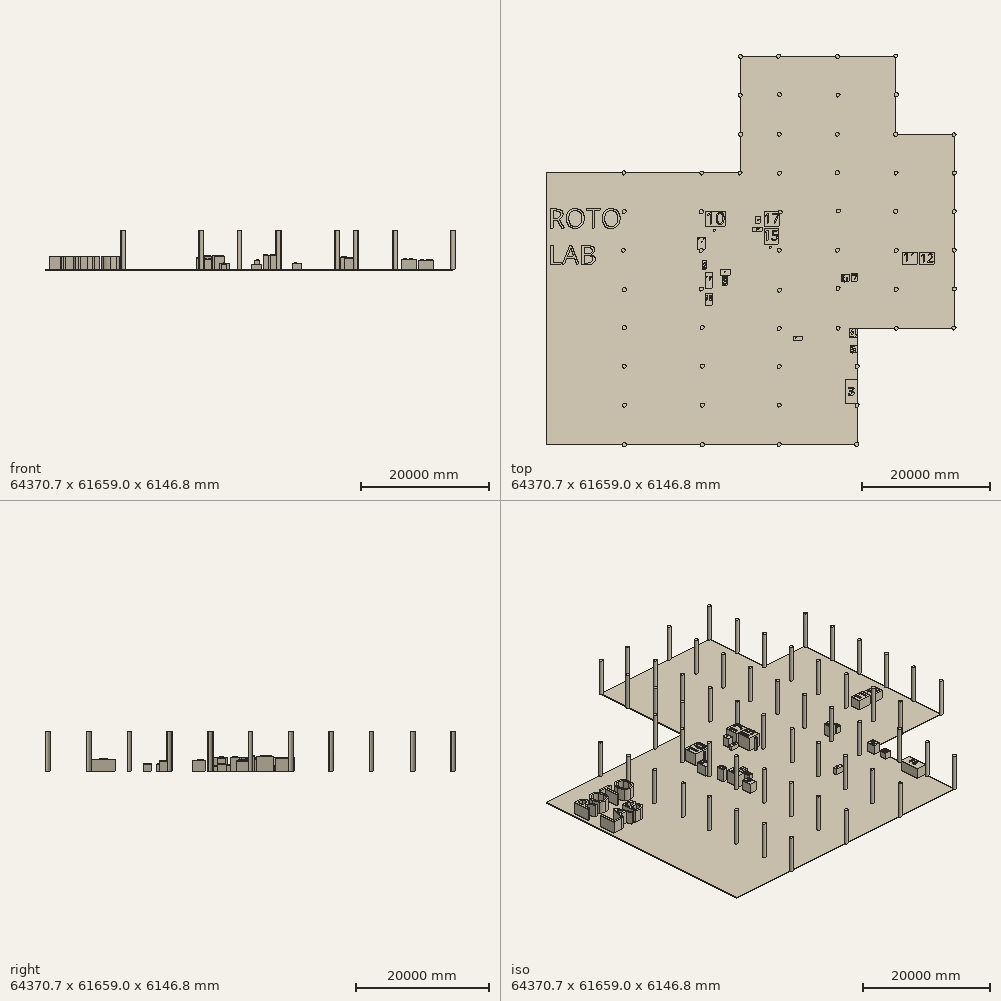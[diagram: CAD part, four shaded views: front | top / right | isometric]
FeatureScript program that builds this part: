
annotation { "Feature Type Name" : "Feature", "Feature Type Description" : "" }
export const myFeature = defineFeature(function(context is Context, id is Id, definition is map)
    precondition{}
    {
        {
            var Q0;
            Q0=qCreatedBy(makeId("Top.planeOp"),FACE);
            var sketch = newSketch(context, id + "F0", { "sketchPlane" : qUnion([Q0])});
            skLineSegment(sketch, "E0", {"start": v(15728, 0) * mm, "end": v(30968, 0) * mm});
            skLineSegment(sketch, "E1", {"start": v(30968, 0) * mm, "end": v(30968, 30480) * mm});
            skLineSegment(sketch, "E2", {"start": v(30968, 30480) * mm, "end": v(21824, 30480) * mm});
            skLineSegment(sketch, "E3", {"start": v(21824, 30480) * mm, "end": v(21824, 42672) * mm});
            skLineSegment(sketch, "E4", {"start": v(-33040, 24384) * mm, "end": v(-33040, 0) * mm});
            skPoint(sketch, "E5", {"position": v(0, 0) * mm});
            skLineSegment(sketch, "E6", {"start": v(-33040, 24384) * mm, "end": v(-2560, 24384) * mm});
            skLineSegment(sketch, "E7", {"start": v(-2560, 24384) * mm, "end": v(-2560, 42672) * mm});
            skLineSegment(sketch, "E8", {"start": v(-2560, 42672) * mm, "end": v(21824, 42672) * mm});
            skLineSegment(sketch, "E9", {"start": v(15728, 0) * mm, "end": v(15728, -18288) * mm});
            skLineSegment(sketch, "E10", {"start": v(15728, -18288) * mm, "end": v(-33040, -18288) * mm});
            skLineSegment(sketch, "E11", {"start": v(-33040, 0) * mm, "end": v(-33040, -18288) * mm});
            skSolve(sketch);
        }
        {
            var Q0;
            Q0 = qSketchRegion(id + "F0", true);
            extrude(context, id + "F1", {"entities" : qUnion([Q0]), "depth" : 50.8 * mm, "offsetDistance" : 25.4 * mm});
        }
        {
            var Q0;
            Q0=makeQuery(id+"F1.opExtrude","CAP_FACE",FACE,{"disambiguationData":[OSD([sQuery(id+"F0.wireOp",EDGE,"E0"),sQuery(id+"F0.wireOp",EDGE,"E1"),sQuery(id+"F0.wireOp",EDGE,"E2"),sQuery(id+"F0.wireOp",EDGE,"E3"),sQuery(id+"F0.wireOp",EDGE,"EMs3Cac7-QPGr-bt8L-WwCN-rmf20JCazhHY"),sQuery(id+"F0.wireOp",EDGE,"psXAcYbY-NMwD-U9ZH-Obsj-Xogxew4PaL97"),sQuery(id+"F0.wireOp",EDGE,"jVNAj40w-TGht-tEG7-xvlJ-PyNoEMkw6fTJ"),sQuery(id+"F0.wireOp",EDGE,"E4")])],"isStart":false});
            var sketch = newSketch(context, id + "F2", { "sketchPlane" : qUnion([Q0])});
            skText(sketch, "E12", { "text": "ROTO \nLAB", "fontName": "OpenSans-Regular.ttf"});
            const initialGuessF2  = {"E12": [-32.77265, 15.6997, 1, 0, 3.04753]};
            skSetInitialGuess(sketch, initialGuessF2);
            skSolve(sketch);
        }
        {
            var Q0;
            Q0 = qSketchRegion(id + "F2", true);
            extrude(context, id + "F3", {"entities" : qUnion([Q0]), "depth" : 2057.4 * mm, "offsetDistance" : 25.4 * mm});
        }
        {
            var Q0;
            {var subQ0=sQuery(id+"F0.wireOp",EDGE,"E2");var subQ1=sQuery(id+"F0.wireOp",EDGE,"E4");var subQ2=sQuery(id+"F0.wireOp",EDGE,"jVNAj40w-TGht-tEG7-xvlJ-PyNoEMkw6fTJ");var subQ3=sQuery(id+"F0.wireOp",EDGE,"psXAcYbY-NMwD-U9ZH-Obsj-Xogxew4PaL97");var subQ4=sQuery(id+"F0.wireOp",EDGE,"EMs3Cac7-QPGr-bt8L-WwCN-rmf20JCazhHY");var subQ5=sQuery(id+"F0.wireOp",EDGE,"E0");var subQ6=sQuery(id+"F0.wireOp",EDGE,"E3");var subQ7=sQuery(id+"F0.wireOp",EDGE,"E1");Q0=makeQuery(id+"F3.boolean.opBoolean","SPLIT",FACE,{"disambiguationData":[TD([makeQuery(id+"F1.opExtrude","SWEPT_FACE",FACE,{"disambiguationData":[OSD([subQ5])]})])],"derivedFrom":makeQuery(id+"F1.opExtrude","CAP_FACE",FACE,{"disambiguationData":[OSD([subQ5,subQ7,subQ0,subQ6,subQ4,subQ3,subQ2,subQ1])],"isStart":false})});}
            var sketch = newSketch(context, id + "F4", { "sketchPlane" : qUnion([Q0])});
            skPoint(sketch, "E13", {"position": v(-20848, 6096) * mm});
            skPoint(sketch, "E14", {"position": v(-20848, 12192) * mm});
            skPoint(sketch, "E15", {"position": v(-20848, 18288) * mm});
            skPoint(sketch, "E16.middle", {"position": v(-20848, 24384) * mm});
            skPoint(sketch, "E17.MirrorP", {"position": v(-8656, 24384) * mm});
            skPoint(sketch, "E18.MirrorP", {"position": v(-8656, 18288) * mm});
            skPoint(sketch, "E19.MirrorP", {"position": v(-8656, 12192) * mm});
            skPoint(sketch, "E20.MirrorP", {"position": v(-8656, 6096) * mm});
            skPoint(sketch, "E21", {"position": v(-2560, 24384) * mm});
            skPoint(sketch, "E22", {"position": v(-2560, 30480) * mm});
            skPoint(sketch, "E23", {"position": v(-2560, 36576) * mm});
            skPoint(sketch, "E24", {"position": v(-2560, 42672) * mm});
            skPoint(sketch, "E25.MirrorP", {"position": v(3536, 24384) * mm});
            skPoint(sketch, "E26.MirrorP", {"position": v(3536, 18288) * mm});
            skPoint(sketch, "E27.MirrorP", {"position": v(3536, 12192) * mm});
            skPoint(sketch, "E28.MirrorP", {"position": v(3536, 6096) * mm});
            skPoint(sketch, "E29.MirrorP", {"position": v(-2538.5, 30490.61) * mm});
            skPoint(sketch, "E30.MirrorP", {"position": v(-2618.75, 36589.82) * mm});
            skPoint(sketch, "E31.MirrorP", {"position": v(-2567.19, 42656.06) * mm});
            skPoint(sketch, "E32", {"position": v(3536, 30487.97) * mm});
            skPoint(sketch, "E33", {"position": v(3536, 36576) * mm});
            skPoint(sketch, "E34", {"position": v(3536, 42672) * mm});
            skPoint(sketch, "E35", {"position": v(30968, 0) * mm});
            skPoint(sketch, "E36", {"position": v(12680, 36576) * mm});
            skPoint(sketch, "E37", {"position": v(12680, 30483.98) * mm});
            skPoint(sketch, "E38", {"position": v(12680, 24384) * mm});
            skPoint(sketch, "E39", {"position": v(12680, 18288) * mm});
            skPoint(sketch, "E40", {"position": v(12680, 12192) * mm});
            skPoint(sketch, "E41", {"position": v(12680, 6096) * mm});
            skPoint(sketch, "E42", {"position": v(21824, 6096) * mm});
            skPoint(sketch, "E43", {"position": v(21824, 12192) * mm});
            skPoint(sketch, "E44", {"position": v(21824, 18288) * mm});
            skPoint(sketch, "E45", {"position": v(21824, 24384) * mm});
            skPoint(sketch, "E46", {"position": v(21824, 36576) * mm});
            skPoint(sketch, "E47", {"position": v(21824, 42672) * mm});
            skPoint(sketch, "E48", {"position": v(30968, 30480) * mm});
            skPoint(sketch, "E49", {"position": v(30968, 24384) * mm});
            skPoint(sketch, "E50.MirrorP", {"position": v(3550.78, 30482.18) * mm});
            skPoint(sketch, "E51.MirrorP", {"position": v(3476.16, 36549.2) * mm});
            skPoint(sketch, "E52.MirrorP", {"position": v(3533.6, 42706.6) * mm});
            skPoint(sketch, "E53.MirrorP", {"position": v(12678, 36632.63) * mm});
            skPoint(sketch, "E54", {"position": v(12680, 42672) * mm});
            skPoint(sketch, "E55.MirrorP", {"position": v(12678.61, 42676.51) * mm});
            skPoint(sketch, "E56.MirrorP", {"position": v(12678.59, 30476.38) * mm});
            skPoint(sketch, "E57.MirrorP", {"position": v(12637.8, 24336.72) * mm});
            skPoint(sketch, "E58.MirrorP", {"position": v(12677.36, 18237.22) * mm});
            skPoint(sketch, "E59.MirrorP", {"position": v(12716.92, 12057.46) * mm});
            skPoint(sketch, "E60.MirrorP", {"position": v(12676.14, 6038.18) * mm});
            skPoint(sketch, "E61.MirrorP", {"position": v(12675.55, 99.18) * mm});
            skPoint(sketch, "E62.MirrorP", {"position": v(21795.62, -57.69) * mm});
            skPoint(sketch, "E63.MirrorP", {"position": v(30955.9, -54.02) * mm});
            skPoint(sketch, "E64", {"position": v(30968, 6096) * mm});
            skPoint(sketch, "E65", {"position": v(30968, 12192) * mm});
            skPoint(sketch, "E66", {"position": v(30968, 18288) * mm});
            skPoint(sketch, "E67.MirrorP", {"position": v(21789.02, 6025.7) * mm});
            skPoint(sketch, "E68.MirrorP", {"position": v(21885.2, 12157.88) * mm});
            skPoint(sketch, "E69.MirrorP", {"position": v(21838.03, 18290) * mm});
            skPoint(sketch, "E70.MirrorP", {"position": v(21790.86, 24374.41) * mm});
            skPoint(sketch, "E71", {"position": v(21824, 30480) * mm});
            skPoint(sketch, "E72.MirrorP", {"position": v(21839.24, 30458.86) * mm});
            skPoint(sketch, "E73.MirrorP", {"position": v(21839.86, 36591) * mm});
            skPoint(sketch, "E74.MirrorP", {"position": v(21803.1, 42617.52) * mm});
            skPoint(sketch, "E75.MirrorP", {"position": v(30931.19, 30439.54) * mm});
            skPoint(sketch, "E76.MirrorP", {"position": v(30930.57, 24310.52) * mm});
            skPoint(sketch, "E77.MirrorP", {"position": v(30929.96, 18209.88) * mm});
            skPoint(sketch, "E78.MirrorP", {"position": v(30900.96, 12279.48) * mm});
            skPoint(sketch, "E79.MirrorP", {"position": v(30957.16, 6065.37) * mm});
            skCircle(sketch, "E80", {"center": v(-20799.6, 6015.66) * mm, "radius": 317.5 * mm});
            skCircle(sketch, "E81", {"center": v(-20946.7, 12207.64) * mm, "radius": 317.5 * mm});
            skCircle(sketch, "E82", {"center": v(-20800.82, 18305.22) * mm, "radius": 317.5 * mm});
            skCircle(sketch, "E83", {"center": v(-20859.17, 24373.64) * mm, "radius": 317.5 * mm});
            skCircle(sketch, "E84", {"center": v(-8556.08, 84.7) * mm, "radius": 317.5 * mm});
            skCircle(sketch, "E85", {"center": v(-8721.12, 6149.9) * mm, "radius": 317.5 * mm});
            skCircle(sketch, "E86", {"center": v(-8762.38, 12173.82) * mm, "radius": 317.5 * mm});
            skCircle(sketch, "E87", {"center": v(-8721.12, 18280.26) * mm, "radius": 317.5 * mm});
            skCircle(sketch, "E88", {"center": v(-8638.6, 24345.45) * mm, "radius": 317.5 * mm});
            skCircle(sketch, "E89", {"center": v(-2655.93, 24345.45) * mm, "radius": 317.5 * mm});
            skCircle(sketch, "E90", {"center": v(-2532.15, 30410.63) * mm, "radius": 317.5 * mm});
            skCircle(sketch, "E91", {"center": v(-2614.67, 36558.34) * mm, "radius": 317.5 * mm});
            skCircle(sketch, "E92", {"center": v(-2532.15, 42623.52) * mm, "radius": 317.5 * mm});
            skCircle(sketch, "E93", {"center": v(3409.25, 42706.04) * mm, "radius": 317.5 * mm});
            skCircle(sketch, "E94", {"center": v(3574.3, 36640.86) * mm, "radius": 317.5 * mm});
            skCircle(sketch, "E95", {"center": v(3491.77, 30451.9) * mm, "radius": 317.5 * mm});
            skCircle(sketch, "E96", {"center": v(3574.3, 24304.19) * mm, "radius": 317.5 * mm});
            skCircle(sketch, "E97", {"center": v(3656.81, 18239) * mm, "radius": 317.5 * mm});
            skCircle(sketch, "E98", {"center": v(3491.77, 12256.34) * mm, "radius": 317.5 * mm});
            skCircle(sketch, "E99", {"center": v(3574.3, 5984.85) * mm, "radius": 317.5 * mm});
            skCircle(sketch, "E100", {"center": v(3491.77, -80.33) * mm, "radius": 317.5 * mm});
            skCircle(sketch, "E101", {"center": v(12733.96, 2.19) * mm, "radius": 317.5 * mm});
            skCircle(sketch, "E102", {"center": v(12733.96, 6273.67) * mm, "radius": 317.5 * mm});
            skCircle(sketch, "E103", {"center": v(12692.7, 12256.34) * mm, "radius": 317.5 * mm});
            skCircle(sketch, "E104", {"center": v(12816.48, 18404.04) * mm, "radius": 317.5 * mm});
            skCircle(sketch, "E105", {"center": v(12651.44, 24386.7) * mm, "radius": 317.5 * mm});
            skCircle(sketch, "E106", {"center": v(12651.44, 30410.63) * mm, "radius": 317.5 * mm});
            skCircle(sketch, "E107", {"center": v(12752.19, 36600.89) * mm, "radius": 317.5 * mm});
            skCircle(sketch, "E108", {"center": v(12653.7, 42639.29) * mm, "radius": 317.5 * mm});
            skCircle(sketch, "E109", {"center": v(21813.25, 42717.7) * mm, "radius": 317.5 * mm});
            skCircle(sketch, "E110", {"center": v(21886.85, 36633.47) * mm, "radius": 317.5 * mm});
            skCircle(sketch, "E111", {"center": v(21813.25, 30402.04) * mm, "radius": 317.5 * mm});
            skCircle(sketch, "E112", {"center": v(30964.14, 30352.98) * mm, "radius": 317.5 * mm});
            skCircle(sketch, "E113", {"center": v(21837.78, 24366.87) * mm, "radius": 317.5 * mm});
            skCircle(sketch, "E114", {"center": v(21788.72, 18331.7) * mm, "radius": 317.5 * mm});
            skCircle(sketch, "E115", {"center": v(31013.2, 24366.87) * mm, "radius": 317.5 * mm});
            skCircle(sketch, "E116", {"center": v(30988.67, 18307.17) * mm, "radius": 317.5 * mm});
            skCircle(sketch, "E117", {"center": v(21886.85, 12173.87) * mm, "radius": 317.5 * mm});
            skCircle(sketch, "E118", {"center": v(30964.13, 12247.47) * mm, "radius": 317.5 * mm});
            skCircle(sketch, "E119", {"center": v(21862.32, 6065.1) * mm, "radius": 317.5 * mm});
            skCircle(sketch, "E120", {"center": v(31013.2, 6163.24) * mm, "radius": 317.5 * mm});
            skCircle(sketch, "E121", {"center": v(21911.38, -19.13) * mm, "radius": 317.5 * mm});
            skCircle(sketch, "E122", {"center": v(30939.6, 5.4) * mm, "radius": 317.5 * mm});
            skLineSegment(sketch, "E123", {"start": v(-20799.6, 6015.66) * mm, "end": v(-20799.6, -23105.73) * mm, "construction": true});
            skLineSegment(sketch, "E124", {"start": v(-8556.08, 84.7) * mm, "end": v(-8556.08, -21895.34) * mm, "construction": true});
            skLineSegment(sketch, "E125", {"start": v(3491.77, -80.33) * mm, "end": v(3491.77, -26208.42) * mm, "construction": true});
            skLineSegment(sketch, "E126", {"start": v(-8556.08, 84.7) * mm, "end": v(-20983, 84.7) * mm, "construction": true});
            skLineSegment(sketch, "E127", {"start": v(-33040, -6011.3) * mm, "end": v(15728, -6011.3) * mm, "construction": true});
            skLineSegment(sketch, "E128", {"start": v(-33040, -12107.3) * mm, "end": v(15728, -12107.3) * mm, "construction": true});
            skCircle(sketch, "E129", {"center": v(-20793.8, 82.6) * mm, "radius": 317.5 * mm});
            skCircle(sketch, "E130", {"center": v(-20807.96, -5984.06) * mm, "radius": 317.5 * mm});
            skCircle(sketch, "E131", {"center": v(-20780.45, -12108.35) * mm, "radius": 317.5 * mm});
            skCircle(sketch, "E132", {"center": v(-20805.76, -18297.2) * mm, "radius": 317.5 * mm});
            skCircle(sketch, "E133", {"center": v(-8567.42, -5956.38) * mm, "radius": 317.5 * mm});
            skCircle(sketch, "E134", {"center": v(-8567.42, -12081.94) * mm, "radius": 317.5 * mm});
            skCircle(sketch, "E135", {"center": v(-8553.38, -18285.04) * mm, "radius": 317.5 * mm});
            skCircle(sketch, "E136", {"center": v(3495.9, -18306.32) * mm, "radius": 317.5 * mm});
            skCircle(sketch, "E137", {"center": v(3490.2, -12072.84) * mm, "radius": 317.5 * mm});
            skCircle(sketch, "E138", {"center": v(3511.49, -6029.21) * mm, "radius": 317.5 * mm});
            skCircle(sketch, "E139", {"center": v(15735.52, -5993.42) * mm, "radius": 317.5 * mm});
            skCircle(sketch, "E140", {"center": v(15717.62, -12096.79) * mm, "radius": 317.5 * mm});
            skCircle(sketch, "E141", {"center": v(15699.72, -18253.85) * mm, "radius": 317.5 * mm});
            skSolve(sketch);
        }
        {
            var Q0;
            Q0 = qSketchRegion(id + "F4", true);
            extrude(context, id + "F5", {"entities" : qUnion([Q0]), "operationType" : NewBodyOperationType.ADD, "depth" : 6096 * mm, "offsetDistance" : 25.4 * mm});
        }
        {
            var Q0;
            {var subQ0=sQuery(id+"F0.wireOp",EDGE,"E2");var subQ1=sQuery(id+"F0.wireOp",EDGE,"E8");var subQ2=sQuery(id+"F0.wireOp",EDGE,"E7");var subQ3=sQuery(id+"F0.wireOp",EDGE,"E6");var subQ4=sQuery(id+"F0.wireOp",EDGE,"E4");var subQ5=sQuery(id+"F0.wireOp",EDGE,"E0");var subQ6=sQuery(id+"F0.wireOp",EDGE,"E3");var subQ7=sQuery(id+"F0.wireOp",EDGE,"E1");Q0=makeQuery(id+"F3.boolean.opBoolean","SPLIT",FACE,{"disambiguationData":[TD([makeQuery(id+"F1.opExtrude","SWEPT_FACE",FACE,{"disambiguationData":[OSD([subQ5])]})])],"derivedFrom":makeQuery(id+"F1.opExtrude","CAP_FACE",FACE,{"disambiguationData":[OSD([subQ5,subQ7,subQ0,subQ6,subQ4,subQ3,subQ2,subQ1])],"isStart":false})});}
            var sketch = newSketch(context, id + "F6", { "sketchPlane" : qUnion([Q0])});
            skLineSegment(sketch, "E142.bottom", {"start": v(-5719.61, 9235.68) * mm, "end": v(-4195.61, 9235.68) * mm});
            skLineSegment(sketch, "E142.top", {"start": v(-5719.61, 8321.28) * mm, "end": v(-4195.61, 8321.28) * mm});
            skLineSegment(sketch, "E142.left", {"start": v(-5719.61, 9235.68) * mm, "end": v(-5719.61, 8321.28) * mm});
            skLineSegment(sketch, "E142.right", {"start": v(-4195.61, 9235.68) * mm, "end": v(-4195.61, 8321.28) * mm});
            skSolve(sketch);
        }
        {
            var Q0;
            Q0 = qSketchRegion(id + "F6", true);
            extrude(context, id + "F7", {"entities" : qUnion([Q0]), "depth" : 990.6 * mm, "offsetDistance" : 25.4 * mm});
        }
        {
            var Q0;
            {var subQ0=sQuery(id+"F0.wireOp",EDGE,"E2");var subQ1=sQuery(id+"F0.wireOp",EDGE,"E8");var subQ2=sQuery(id+"F0.wireOp",EDGE,"E7");var subQ3=sQuery(id+"F0.wireOp",EDGE,"E6");var subQ4=sQuery(id+"F0.wireOp",EDGE,"E4");var subQ5=sQuery(id+"F0.wireOp",EDGE,"E0");var subQ6=sQuery(id+"F0.wireOp",EDGE,"E3");var subQ7=sQuery(id+"F0.wireOp",EDGE,"E1");Q0=makeQuery(id+"F3.boolean.opBoolean","SPLIT",FACE,{"disambiguationData":[TD([makeQuery(id+"F1.opExtrude","SWEPT_FACE",FACE,{"disambiguationData":[OSD([subQ5])]})])],"derivedFrom":makeQuery(id+"F1.opExtrude","CAP_FACE",FACE,{"disambiguationData":[OSD([subQ5,subQ7,subQ0,subQ6,subQ4,subQ3,subQ2,subQ1])],"isStart":false})});}
            var sketch = newSketch(context, id + "F8", { "sketchPlane" : qUnion([Q0])});
            skLineSegment(sketch, "E143.bottom", {"start": v(-8590.4, 10569.5) * mm, "end": v(-7853.8, 10569.5) * mm});
            skLineSegment(sketch, "E143.top", {"start": v(-8590.4, 9172.5) * mm, "end": v(-7853.8, 9172.5) * mm});
            skLineSegment(sketch, "E143.left", {"start": v(-8590.4, 10569.5) * mm, "end": v(-8590.4, 9172.5) * mm});
            skLineSegment(sketch, "E143.right", {"start": v(-7853.8, 10569.5) * mm, "end": v(-7853.8, 9172.5) * mm});
            skSolve(sketch);
        }
        {
            var Q0;
            {var subQ0=sQuery(id+"F0.wireOp",EDGE,"E9");var subQ1=sQuery(id+"F0.wireOp",EDGE,"E8");var subQ2=sQuery(id+"F0.wireOp",EDGE,"E7");var subQ3=sQuery(id+"F0.wireOp",EDGE,"E6");var subQ4=sQuery(id+"F0.wireOp",EDGE,"E11");var subQ5=sQuery(id+"F0.wireOp",EDGE,"E4");var subQ6=sQuery(id+"F0.wireOp",EDGE,"E10");var subQ7=sQuery(id+"F0.wireOp",EDGE,"E0");var subQ8=sQuery(id+"F0.wireOp",EDGE,"E3");var subQ9=sQuery(id+"F0.wireOp",EDGE,"E1");var subQ10=sQuery(id+"F0.wireOp",EDGE,"E2");Q0=makeQuery(id+"F3.boolean.opBoolean","SPLIT",FACE,{"disambiguationData":[TD([makeQuery(id+"F1.opExtrude","SWEPT_FACE",FACE,{"disambiguationData":[OSD([subQ7])]})])],"derivedFrom":makeQuery(id+"F1.opExtrude","CAP_FACE",FACE,{"disambiguationData":[OSD([subQ7,subQ9,subQ10,subQ8,subQ5,subQ3,subQ2,subQ1,subQ0,subQ6,subQ4])],"isStart":false})});}
            var sketch = newSketch(context, id + "F9", { "sketchPlane" : qUnion([Q0])});
            skLineSegment(sketch, "E144.bottom", {"start": v(13899.2, -8121.86) * mm, "end": v(15728, -8121.86) * mm});
            skLineSegment(sketch, "E144.top", {"start": v(13899.2, -11779.46) * mm, "end": v(15728, -11779.46) * mm});
            skLineSegment(sketch, "E144.left", {"start": v(13899.2, -8121.86) * mm, "end": v(13899.2, -11779.46) * mm});
            skLineSegment(sketch, "E144.right", {"start": v(15728, -8121.86) * mm, "end": v(15728, -11779.46) * mm});
            skSolve(sketch);
        }
        {
            var Q0;
            Q0 = qSketchRegion(id + "F9", true);
            extrude(context, id + "F10", {"entities" : qUnion([Q0]), "depth" : 1778 * mm, "offsetDistance" : 25.4 * mm});
        }
        {
            var Q0;
            {var subQ0=sQuery(id+"F0.wireOp",EDGE,"E9");var subQ1=sQuery(id+"F0.wireOp",EDGE,"E8");var subQ2=sQuery(id+"F0.wireOp",EDGE,"E7");var subQ3=sQuery(id+"F0.wireOp",EDGE,"E6");var subQ4=sQuery(id+"F0.wireOp",EDGE,"E11");var subQ5=sQuery(id+"F0.wireOp",EDGE,"E4");var subQ6=sQuery(id+"F0.wireOp",EDGE,"E10");var subQ7=sQuery(id+"F0.wireOp",EDGE,"E0");var subQ8=sQuery(id+"F0.wireOp",EDGE,"E3");var subQ9=sQuery(id+"F0.wireOp",EDGE,"E1");var subQ10=sQuery(id+"F0.wireOp",EDGE,"E2");Q0=makeQuery(id+"F3.boolean.opBoolean","SPLIT",FACE,{"disambiguationData":[TD([makeQuery(id+"F1.opExtrude","SWEPT_FACE",FACE,{"disambiguationData":[OSD([subQ7])]})])],"derivedFrom":makeQuery(id+"F1.opExtrude","CAP_FACE",FACE,{"disambiguationData":[OSD([subQ7,subQ9,subQ10,subQ8,subQ5,subQ3,subQ2,subQ1,subQ0,subQ6,subQ4])],"isStart":false})});}
            var sketch = newSketch(context, id + "F11", { "sketchPlane" : qUnion([Q0])});
            skLineSegment(sketch, "E145.bottom", {"start": v(14508.8, 0) * mm, "end": v(15728, 0) * mm});
            skLineSegment(sketch, "E145.top", {"start": v(14508.8, -1524) * mm, "end": v(15728, -1524) * mm});
            skLineSegment(sketch, "E145.left", {"start": v(14508.8, 0) * mm, "end": v(14508.8, -1524) * mm});
            skLineSegment(sketch, "E145.right", {"start": v(15728, 0) * mm, "end": v(15728, -1524) * mm});
            skSolve(sketch);
        }
        {
            var Q0;
            Q0 = qSketchRegion(id + "F11", true);
            extrude(context, id + "F12", {"entities" : qUnion([Q0]), "depth" : 1524 * mm, "offsetDistance" : 25.4 * mm});
        }
        {
            var Q0;
            {var subQ0=sQuery(id+"F0.wireOp",EDGE,"E9");var subQ1=sQuery(id+"F0.wireOp",EDGE,"E8");var subQ2=sQuery(id+"F0.wireOp",EDGE,"E7");var subQ3=sQuery(id+"F0.wireOp",EDGE,"E6");var subQ4=sQuery(id+"F0.wireOp",EDGE,"E11");var subQ5=sQuery(id+"F0.wireOp",EDGE,"E4");var subQ6=sQuery(id+"F0.wireOp",EDGE,"E10");var subQ7=sQuery(id+"F0.wireOp",EDGE,"E0");var subQ8=sQuery(id+"F0.wireOp",EDGE,"E3");var subQ9=sQuery(id+"F0.wireOp",EDGE,"E1");var subQ10=sQuery(id+"F0.wireOp",EDGE,"E2");Q0=makeQuery(id+"F3.boolean.opBoolean","SPLIT",FACE,{"disambiguationData":[TD([makeQuery(id+"F1.opExtrude","SWEPT_FACE",FACE,{"disambiguationData":[OSD([subQ7])]})])],"derivedFrom":makeQuery(id+"F1.opExtrude","CAP_FACE",FACE,{"disambiguationData":[OSD([subQ7,subQ9,subQ10,subQ8,subQ5,subQ3,subQ2,subQ1,subQ0,subQ6,subQ4])],"isStart":false})});}
            var sketch = newSketch(context, id + "F13", { "sketchPlane" : qUnion([Q0])});
            skLineSegment(sketch, "E146.bottom", {"start": v(14661.2, -2731.45) * mm, "end": v(15728, -2731.45) * mm});
            skLineSegment(sketch, "E146.top", {"start": v(14661.2, -3874.45) * mm, "end": v(15728, -3874.45) * mm});
            skLineSegment(sketch, "E146.left", {"start": v(14661.2, -2731.45) * mm, "end": v(14661.2, -3874.45) * mm});
            skLineSegment(sketch, "E146.right", {"start": v(15728, -2731.45) * mm, "end": v(15728, -3874.45) * mm});
            skSolve(sketch);
        }
        {
            var Q0;
            Q0 = qSketchRegion(id + "F13", true);
            extrude(context, id + "F14", {"entities" : qUnion([Q0]), "depth" : 1041.4 * mm, "offsetDistance" : 25.4 * mm});
        }
        {
            var Q0;
            {var subQ0=sQuery(id+"F0.wireOp",EDGE,"E9");var subQ1=sQuery(id+"F0.wireOp",EDGE,"E8");var subQ2=sQuery(id+"F0.wireOp",EDGE,"E7");var subQ3=sQuery(id+"F0.wireOp",EDGE,"E6");var subQ4=sQuery(id+"F0.wireOp",EDGE,"E11");var subQ5=sQuery(id+"F0.wireOp",EDGE,"E4");var subQ6=sQuery(id+"F0.wireOp",EDGE,"E10");var subQ7=sQuery(id+"F0.wireOp",EDGE,"E0");var subQ8=sQuery(id+"F0.wireOp",EDGE,"E3");var subQ9=sQuery(id+"F0.wireOp",EDGE,"E1");var subQ10=sQuery(id+"F0.wireOp",EDGE,"E2");Q0=makeQuery(id+"F3.boolean.opBoolean","SPLIT",FACE,{"disambiguationData":[TD([makeQuery(id+"F1.opExtrude","SWEPT_FACE",FACE,{"disambiguationData":[OSD([subQ7])]})])],"derivedFrom":makeQuery(id+"F1.opExtrude","CAP_FACE",FACE,{"disambiguationData":[OSD([subQ7,subQ9,subQ10,subQ8,subQ5,subQ3,subQ2,subQ1,subQ0,subQ6,subQ4])],"isStart":false})});}
            var sketch = newSketch(context, id + "F15", { "sketchPlane" : qUnion([Q0])});
            skLineSegment(sketch, "E147.bottom", {"start": v(13343.47, 7272.04) * mm, "end": v(14562.67, 7272.04) * mm});
            skLineSegment(sketch, "E147.top", {"start": v(13343.47, 8491.24) * mm, "end": v(14562.67, 8491.24) * mm});
            skLineSegment(sketch, "E147.left", {"start": v(13343.47, 7272.04) * mm, "end": v(13343.47, 8491.24) * mm});
            skLineSegment(sketch, "E147.right", {"start": v(14562.67, 7272.04) * mm, "end": v(14562.67, 8491.24) * mm});
            skSolve(sketch);
        }
        {
            var Q0;
            Q0 = qSketchRegion(id + "F15", true);
            extrude(context, id + "F16", {"entities" : qUnion([Q0]), "depth" : 1905 * mm, "offsetDistance" : 25.4 * mm});
        }
        {
            var Q0;
            {var subQ0=sQuery(id+"F0.wireOp",EDGE,"E9");var subQ1=sQuery(id+"F0.wireOp",EDGE,"E8");var subQ2=sQuery(id+"F0.wireOp",EDGE,"E7");var subQ3=sQuery(id+"F0.wireOp",EDGE,"E6");var subQ4=sQuery(id+"F0.wireOp",EDGE,"E11");var subQ5=sQuery(id+"F0.wireOp",EDGE,"E4");var subQ6=sQuery(id+"F0.wireOp",EDGE,"E10");var subQ7=sQuery(id+"F0.wireOp",EDGE,"E0");var subQ8=sQuery(id+"F0.wireOp",EDGE,"E3");var subQ9=sQuery(id+"F0.wireOp",EDGE,"E1");var subQ10=sQuery(id+"F0.wireOp",EDGE,"E2");Q0=makeQuery(id+"F3.boolean.opBoolean","SPLIT",FACE,{"disambiguationData":[TD([makeQuery(id+"F1.opExtrude","SWEPT_FACE",FACE,{"disambiguationData":[OSD([subQ7])]})])],"derivedFrom":makeQuery(id+"F1.opExtrude","CAP_FACE",FACE,{"disambiguationData":[OSD([subQ7,subQ9,subQ10,subQ8,subQ5,subQ3,subQ2,subQ1,subQ0,subQ6,subQ4])],"isStart":false})});}
            var sketch = newSketch(context, id + "F17", { "sketchPlane" : qUnion([Q0])});
            skLineSegment(sketch, "E148.bottom", {"start": v(14902.92, 8525.07) * mm, "end": v(15817.32, 8525.07) * mm});
            skLineSegment(sketch, "E148.top", {"start": v(14902.92, 7305.87) * mm, "end": v(15817.32, 7305.87) * mm});
            skLineSegment(sketch, "E148.left", {"start": v(14902.92, 8525.07) * mm, "end": v(14902.92, 7305.87) * mm});
            skLineSegment(sketch, "E148.right", {"start": v(15817.32, 8525.07) * mm, "end": v(15817.32, 7305.87) * mm});
            skSolve(sketch);
        }
        {
            var Q0;
            Q0=makeQuery(id+"F17.imprint","IMPRINT",FACE,{"disambiguationData":[TD([[makeQuery(id+"F17.imprint","IMPRINT",EDGE,{"derivedFrom":sQuery(id+"F17.wireOp",EDGE,"E148.bottom")}),-1.0]])]});
            extrude(context, id + "F18", {"entities" : qUnion([Q0]), "depth" : 1092.2 * mm, "offsetDistance" : 25.4 * mm});
        }
        {
            var Q0;
            Q0=makeQuery(id+"F8.imprint","IMPRINT",FACE,{"disambiguationData":[TD([[makeQuery(id+"F8.imprint","IMPRINT",EDGE,{"derivedFrom":sQuery(id+"F8.wireOp",EDGE,"E143.bottom")}),-1.0]])]});
            extrude(context, id + "F19", {"entities" : qUnion([Q0]), "depth" : 2184.4 * mm, "offsetDistance" : 25.4 * mm});
        }
        {
            var Q0;
            {var subQ0=sQuery(id+"F0.wireOp",EDGE,"E9");var subQ1=sQuery(id+"F0.wireOp",EDGE,"E8");var subQ2=sQuery(id+"F0.wireOp",EDGE,"E7");var subQ3=sQuery(id+"F0.wireOp",EDGE,"E6");var subQ4=sQuery(id+"F0.wireOp",EDGE,"E11");var subQ5=sQuery(id+"F0.wireOp",EDGE,"E4");var subQ6=sQuery(id+"F0.wireOp",EDGE,"E10");var subQ7=sQuery(id+"F0.wireOp",EDGE,"E0");var subQ8=sQuery(id+"F0.wireOp",EDGE,"E3");var subQ9=sQuery(id+"F0.wireOp",EDGE,"E1");var subQ10=sQuery(id+"F0.wireOp",EDGE,"E2");Q0=makeQuery(id+"F3.boolean.opBoolean","SPLIT",FACE,{"disambiguationData":[TD([makeQuery(id+"F1.opExtrude","SWEPT_FACE",FACE,{"disambiguationData":[OSD([subQ7])]})])],"derivedFrom":makeQuery(id+"F1.opExtrude","CAP_FACE",FACE,{"disambiguationData":[OSD([subQ7,subQ9,subQ10,subQ8,subQ5,subQ3,subQ2,subQ1,subQ0,subQ6,subQ4])],"isStart":false})});}
            var sketch = newSketch(context, id + "F20", { "sketchPlane" : qUnion([Q0])});
            skLineSegment(sketch, "E149.bottom", {"start": v(-5361.74, 8182.09) * mm, "end": v(-4574.34, 8182.09) * mm});
            skLineSegment(sketch, "E149.top", {"start": v(-5361.74, 6658.09) * mm, "end": v(-4574.34, 6658.09) * mm});
            skLineSegment(sketch, "E149.left", {"start": v(-5361.74, 8182.09) * mm, "end": v(-5361.74, 6658.09) * mm});
            skLineSegment(sketch, "E149.right", {"start": v(-4574.34, 8182.09) * mm, "end": v(-4574.34, 6658.09) * mm});
            skSolve(sketch);
        }
        {
            var Q0;
            Q0 = qSketchRegion(id + "F20", true);
            extrude(context, id + "F21", {"entities" : qUnion([Q0]), "depth" : 838.2 * mm, "offsetDistance" : 25.4 * mm});
        }
        {
            var Q0;
            Q0=makeQuery(id+"F1.opExtrude","CAP_FACE",FACE,{"disambiguationData":[OSD([sQuery(id+"F0.wireOp",EDGE,"E0"),sQuery(id+"F0.wireOp",EDGE,"E1"),sQuery(id+"F0.wireOp",EDGE,"E2"),sQuery(id+"F0.wireOp",EDGE,"E3"),sQuery(id+"F0.wireOp",EDGE,"E4"),sQuery(id+"F0.wireOp",EDGE,"E6"),sQuery(id+"F0.wireOp",EDGE,"E7"),sQuery(id+"F0.wireOp",EDGE,"E8"),sQuery(id+"F0.wireOp",EDGE,"E9"),sQuery(id+"F0.wireOp",EDGE,"E10"),sQuery(id+"F0.wireOp",EDGE,"E11")])],"isStart":false});
            var sketch = newSketch(context, id + "F22", { "sketchPlane" : qUnion([Q0])});
            skLineSegment(sketch, "E150.bottom", {"start": v(5661.14, -1274.5) * mm, "end": v(7185.14, -1274.5) * mm});
            skLineSegment(sketch, "E150.top", {"start": v(5661.14, -1884.1) * mm, "end": v(7185.14, -1884.1) * mm});
            skLineSegment(sketch, "E150.left", {"start": v(5661.14, -1274.5) * mm, "end": v(5661.14, -1884.1) * mm});
            skLineSegment(sketch, "E150.right", {"start": v(7185.14, -1274.5) * mm, "end": v(7185.14, -1884.1) * mm});
            skSolve(sketch);
        }
        {
            var Q0;
            Q0 = qSketchRegion(id + "F22", true);
            extrude(context, id + "F23", {"entities" : qUnion([Q0]), "depth" : 1016 * mm, "offsetDistance" : 25.4 * mm});
        }
        {
            var Q0;
            Q0=makeQuery(id+"F1.opExtrude","CAP_FACE",FACE,{"disambiguationData":[OSD([sQuery(id+"F0.wireOp",EDGE,"E0"),sQuery(id+"F0.wireOp",EDGE,"E1"),sQuery(id+"F0.wireOp",EDGE,"E2"),sQuery(id+"F0.wireOp",EDGE,"E3"),sQuery(id+"F0.wireOp",EDGE,"E4"),sQuery(id+"F0.wireOp",EDGE,"E6"),sQuery(id+"F0.wireOp",EDGE,"E7"),sQuery(id+"F0.wireOp",EDGE,"E8"),sQuery(id+"F0.wireOp",EDGE,"E9"),sQuery(id+"F0.wireOp",EDGE,"E10"),sQuery(id+"F0.wireOp",EDGE,"E11")])],"isStart":false});
            var sketch = newSketch(context, id + "F24", { "sketchPlane" : qUnion([Q0])});
            skLineSegment(sketch, "E151.bottom", {"start": v(-8019.62, 18366.4) * mm, "end": v(-4971.62, 18366.4) * mm});
            skLineSegment(sketch, "E151.top", {"start": v(-8019.62, 15928) * mm, "end": v(-4971.62, 15928) * mm});
            skLineSegment(sketch, "E151.left", {"start": v(-8019.62, 18366.4) * mm, "end": v(-8019.62, 15928) * mm});
            skLineSegment(sketch, "E151.right", {"start": v(-4971.62, 18366.4) * mm, "end": v(-4971.62, 15928) * mm});
            skSolve(sketch);
        }
        {
            var Q0;
            Q0 = qSketchRegion(id + "F24", true);
            extrude(context, id + "F25", {"entities" : qUnion([Q0]), "depth" : 2057.4 * mm, "offsetDistance" : 25.4 * mm});
        }
        {
            var Q0;
            Q0=makeQuery(id+"F1.opExtrude","CAP_FACE",FACE,{"disambiguationData":[OSD([sQuery(id+"F0.wireOp",EDGE,"E0"),sQuery(id+"F0.wireOp",EDGE,"E1"),sQuery(id+"F0.wireOp",EDGE,"E2"),sQuery(id+"F0.wireOp",EDGE,"E3"),sQuery(id+"F0.wireOp",EDGE,"E4"),sQuery(id+"F0.wireOp",EDGE,"E6"),sQuery(id+"F0.wireOp",EDGE,"E7"),sQuery(id+"F0.wireOp",EDGE,"E8"),sQuery(id+"F0.wireOp",EDGE,"E9"),sQuery(id+"F0.wireOp",EDGE,"E10"),sQuery(id+"F0.wireOp",EDGE,"E11")])],"isStart":false});
            var sketch = newSketch(context, id + "F26", { "sketchPlane" : qUnion([Q0])});
            skLineSegment(sketch, "E152.bottom", {"start": v(22791.92, 11899.81) * mm, "end": v(25230.32, 11899.81) * mm});
            skLineSegment(sketch, "E152.top", {"start": v(22791.92, 10071.01) * mm, "end": v(25230.32, 10071.01) * mm});
            skLineSegment(sketch, "E152.left", {"start": v(22791.92, 11899.81) * mm, "end": v(22791.92, 10071.01) * mm});
            skLineSegment(sketch, "E152.right", {"start": v(25230.32, 11899.81) * mm, "end": v(25230.32, 10071.01) * mm});
            skSolve(sketch);
        }
        {
            var Q0;
            Q0 = qSketchRegion(id + "F26", true);
            extrude(context, id + "F27", {"entities" : qUnion([Q0]), "depth" : 1651 * mm, "offsetDistance" : 25.4 * mm});
        }
        {
            var Q0;
            Q0=makeQuery(id+"F1.opExtrude","CAP_FACE",FACE,{"disambiguationData":[OSD([sQuery(id+"F0.wireOp",EDGE,"E0"),sQuery(id+"F0.wireOp",EDGE,"E1"),sQuery(id+"F0.wireOp",EDGE,"E2"),sQuery(id+"F0.wireOp",EDGE,"E3"),sQuery(id+"F0.wireOp",EDGE,"E4"),sQuery(id+"F0.wireOp",EDGE,"E6"),sQuery(id+"F0.wireOp",EDGE,"E7"),sQuery(id+"F0.wireOp",EDGE,"E8"),sQuery(id+"F0.wireOp",EDGE,"E9"),sQuery(id+"F0.wireOp",EDGE,"E10"),sQuery(id+"F0.wireOp",EDGE,"E11")])],"isStart":false});
            var sketch = newSketch(context, id + "F28", { "sketchPlane" : qUnion([Q0])});
            skLineSegment(sketch, "E153.bottom", {"start": v(25478.95, 11867.2) * mm, "end": v(27917.35, 11867.2) * mm});
            skLineSegment(sketch, "E153.top", {"start": v(25478.95, 10038.4) * mm, "end": v(27917.35, 10038.4) * mm});
            skLineSegment(sketch, "E153.left", {"start": v(25478.95, 11867.2) * mm, "end": v(25478.95, 10038.4) * mm});
            skLineSegment(sketch, "E153.right", {"start": v(27917.35, 11867.2) * mm, "end": v(27917.35, 10038.4) * mm});
            skSolve(sketch);
        }
        {
            var Q0;
            Q0 = qSketchRegion(id + "F28", true);
            extrude(context, id + "F29", {"entities" : qUnion([Q0]), "depth" : 1473.2 * mm, "offsetDistance" : 25.4 * mm});
        }
        {
            var Q0;
            Q0=makeQuery(id+"F1.opExtrude","CAP_FACE",FACE,{"disambiguationData":[OSD([sQuery(id+"F0.wireOp",EDGE,"E0"),sQuery(id+"F0.wireOp",EDGE,"E1"),sQuery(id+"F0.wireOp",EDGE,"E2"),sQuery(id+"F0.wireOp",EDGE,"E3"),sQuery(id+"F0.wireOp",EDGE,"E4"),sQuery(id+"F0.wireOp",EDGE,"E6"),sQuery(id+"F0.wireOp",EDGE,"E7"),sQuery(id+"F0.wireOp",EDGE,"E8"),sQuery(id+"F0.wireOp",EDGE,"E9"),sQuery(id+"F0.wireOp",EDGE,"E10"),sQuery(id+"F0.wireOp",EDGE,"E11")])],"isStart":false});
            var sketch = newSketch(context, id + "F30", { "sketchPlane" : qUnion([Q0])});
            skLineSegment(sketch, "E154.bottom", {"start": v(-9311.37, 14229.33) * mm, "end": v(-8092.17, 14229.33) * mm});
            skLineSegment(sketch, "E154.top", {"start": v(-9311.37, 12400.53) * mm, "end": v(-8092.17, 12400.53) * mm});
            skLineSegment(sketch, "E154.left", {"start": v(-9311.37, 14229.33) * mm, "end": v(-9311.37, 12400.53) * mm});
            skLineSegment(sketch, "E154.right", {"start": v(-8092.17, 14229.33) * mm, "end": v(-8092.17, 12400.53) * mm});
            skSolve(sketch);
        }
        {
            var Q0;
            Q0 = qSketchRegion(id + "F30", true);
            extrude(context, id + "F31", {"entities" : qUnion([Q0]), "depth" : 1778 * mm, "offsetDistance" : 25.4 * mm});
        }
        {
            var Q0;
            Q0=makeQuery(id+"F1.opExtrude","CAP_FACE",FACE,{"disambiguationData":[OSD([sQuery(id+"F0.wireOp",EDGE,"E0"),sQuery(id+"F0.wireOp",EDGE,"E1"),sQuery(id+"F0.wireOp",EDGE,"E2"),sQuery(id+"F0.wireOp",EDGE,"E3"),sQuery(id+"F0.wireOp",EDGE,"E4"),sQuery(id+"F0.wireOp",EDGE,"E6"),sQuery(id+"F0.wireOp",EDGE,"E7"),sQuery(id+"F0.wireOp",EDGE,"E8"),sQuery(id+"F0.wireOp",EDGE,"E9"),sQuery(id+"F0.wireOp",EDGE,"E10"),sQuery(id+"F0.wireOp",EDGE,"E11")])],"isStart":false});
            var sketch = newSketch(context, id + "F32", { "sketchPlane" : qUnion([Q0])});
            skLineSegment(sketch, "E155.bottom", {"start": v(1224.85, 15605.8) * mm, "end": v(3358.45, 15605.8) * mm});
            skLineSegment(sketch, "E155.top", {"start": v(1224.85, 13167.4) * mm, "end": v(3358.45, 13167.4) * mm});
            skLineSegment(sketch, "E155.left", {"start": v(1224.85, 15605.8) * mm, "end": v(1224.85, 13167.4) * mm});
            skLineSegment(sketch, "E155.right", {"start": v(3358.45, 15605.8) * mm, "end": v(3358.45, 13167.4) * mm});
            skSolve(sketch);
        }
        {
            var Q0;
            Q0 = qSketchRegion(id + "F32", true);
            extrude(context, id + "F33", {"entities" : qUnion([Q0]), "depth" : 2286 * mm, "offsetDistance" : 25.4 * mm});
        }
        {
            var Q0;
            Q0=makeQuery(id+"F1.opExtrude","CAP_FACE",FACE,{"disambiguationData":[OSD([sQuery(id+"F0.wireOp",EDGE,"E0"),sQuery(id+"F0.wireOp",EDGE,"E1"),sQuery(id+"F0.wireOp",EDGE,"E2"),sQuery(id+"F0.wireOp",EDGE,"E3"),sQuery(id+"F0.wireOp",EDGE,"E4"),sQuery(id+"F0.wireOp",EDGE,"E6"),sQuery(id+"F0.wireOp",EDGE,"E7"),sQuery(id+"F0.wireOp",EDGE,"E8"),sQuery(id+"F0.wireOp",EDGE,"E9"),sQuery(id+"F0.wireOp",EDGE,"E10"),sQuery(id+"F0.wireOp",EDGE,"E11")])],"isStart":false});
            var sketch = newSketch(context, id + "F34", { "sketchPlane" : qUnion([Q0])});
            skLineSegment(sketch, "E156.bottom", {"start": v(-672, 15848.04) * mm, "end": v(852, 15848.04) * mm});
            skLineSegment(sketch, "E156.top", {"start": v(-672, 15238.44) * mm, "end": v(852, 15238.44) * mm});
            skLineSegment(sketch, "E156.left", {"start": v(-672, 15848.04) * mm, "end": v(-672, 15238.44) * mm});
            skLineSegment(sketch, "E156.right", {"start": v(852, 15848.04) * mm, "end": v(852, 15238.44) * mm});
            skSolve(sketch);
        }
        {
            var Q0;
            Q0 = qSketchRegion(id + "F34", true);
            extrude(context, id + "F35", {"entities" : qUnion([Q0]), "depth" : 762 * mm, "offsetDistance" : 25.4 * mm});
        }
        {
            var Q0;
            Q0=makeQuery(id+"F1.opExtrude","CAP_FACE",FACE,{"disambiguationData":[OSD([sQuery(id+"F0.wireOp",EDGE,"E0"),sQuery(id+"F0.wireOp",EDGE,"E1"),sQuery(id+"F0.wireOp",EDGE,"E2"),sQuery(id+"F0.wireOp",EDGE,"E3"),sQuery(id+"F0.wireOp",EDGE,"E4"),sQuery(id+"F0.wireOp",EDGE,"E6"),sQuery(id+"F0.wireOp",EDGE,"E7"),sQuery(id+"F0.wireOp",EDGE,"E8"),sQuery(id+"F0.wireOp",EDGE,"E9"),sQuery(id+"F0.wireOp",EDGE,"E10"),sQuery(id+"F0.wireOp",EDGE,"E11")])],"isStart":false});
            var sketch = newSketch(context, id + "F36", { "sketchPlane" : qUnion([Q0])});
            skLineSegment(sketch, "E157.bottom", {"start": v(-8146.07, 5381.36) * mm, "end": v(-6926.87, 5381.36) * mm});
            skLineSegment(sketch, "E157.top", {"start": v(-8146.07, 3552.56) * mm, "end": v(-6926.87, 3552.56) * mm});
            skLineSegment(sketch, "E157.left", {"start": v(-8146.07, 5381.36) * mm, "end": v(-8146.07, 3552.56) * mm});
            skLineSegment(sketch, "E157.right", {"start": v(-6926.87, 5381.36) * mm, "end": v(-6926.87, 3552.56) * mm});
            skSolve(sketch);
        }
        {
            var Q0;
            Q0 = qSketchRegion(id + "F36", true);
            extrude(context, id + "F37", {"entities" : qUnion([Q0]), "depth" : 1625.6 * mm, "offsetDistance" : 25.4 * mm});
        }
        {
            var Q0;
            Q0=makeQuery(id+"F1.opExtrude","CAP_FACE",FACE,{"disambiguationData":[OSD([sQuery(id+"F0.wireOp",EDGE,"E0"),sQuery(id+"F0.wireOp",EDGE,"E1"),sQuery(id+"F0.wireOp",EDGE,"E2"),sQuery(id+"F0.wireOp",EDGE,"E3"),sQuery(id+"F0.wireOp",EDGE,"E4"),sQuery(id+"F0.wireOp",EDGE,"E6"),sQuery(id+"F0.wireOp",EDGE,"E7"),sQuery(id+"F0.wireOp",EDGE,"E8"),sQuery(id+"F0.wireOp",EDGE,"E9"),sQuery(id+"F0.wireOp",EDGE,"E10"),sQuery(id+"F0.wireOp",EDGE,"E11")])],"isStart":false});
            var sketch = newSketch(context, id + "F38", { "sketchPlane" : qUnion([Q0])});
            skLineSegment(sketch, "E158.bottom", {"start": v(1177.7, 18375.05) * mm, "end": v(3616.1, 18375.05) * mm});
            skLineSegment(sketch, "E158.top", {"start": v(1177.7, 15936.65) * mm, "end": v(3616.1, 15936.65) * mm});
            skLineSegment(sketch, "E158.left", {"start": v(1177.7, 18375.05) * mm, "end": v(1177.7, 15936.65) * mm});
            skLineSegment(sketch, "E158.right", {"start": v(3616.1, 18375.05) * mm, "end": v(3616.1, 15936.65) * mm});
            skSolve(sketch);
        }
        {
            var Q0;
            Q0 = qSketchRegion(id + "F38", true);
            extrude(context, id + "F39", {"entities" : qUnion([Q0]), "depth" : 2032 * mm, "offsetDistance" : 25.4 * mm});
        }
        {
            var Q0;
            Q0=makeQuery(id+"F1.opExtrude","CAP_FACE",FACE,{"disambiguationData":[OSD([sQuery(id+"F0.wireOp",EDGE,"E0"),sQuery(id+"F0.wireOp",EDGE,"E1"),sQuery(id+"F0.wireOp",EDGE,"E2"),sQuery(id+"F0.wireOp",EDGE,"E3"),sQuery(id+"F0.wireOp",EDGE,"E4"),sQuery(id+"F0.wireOp",EDGE,"E6"),sQuery(id+"F0.wireOp",EDGE,"E7"),sQuery(id+"F0.wireOp",EDGE,"E8"),sQuery(id+"F0.wireOp",EDGE,"E9"),sQuery(id+"F0.wireOp",EDGE,"E10"),sQuery(id+"F0.wireOp",EDGE,"E11")])],"isStart":false});
            var sketch = newSketch(context, id + "F40", { "sketchPlane" : qUnion([Q0])});
            skLineSegment(sketch, "E159.bottom", {"start": v(-287.27, 17594.45) * mm, "end": v(627.13, 17594.45) * mm});
            skLineSegment(sketch, "E159.top", {"start": v(-287.27, 16375.25) * mm, "end": v(627.13, 16375.25) * mm});
            skLineSegment(sketch, "E159.left", {"start": v(-287.27, 17594.45) * mm, "end": v(-287.27, 16375.25) * mm});
            skLineSegment(sketch, "E159.right", {"start": v(627.13, 17594.45) * mm, "end": v(627.13, 16375.25) * mm});
            skSolve(sketch);
        }
        {
            var Q0;
            Q0 = qSketchRegion(id + "F40", true);
            extrude(context, id + "F41", {"entities" : qUnion([Q0]), "depth" : 1524 * mm, "offsetDistance" : 25.4 * mm});
        }
        {
            var Q0;
            Q0=makeQuery(id+"F1.opExtrude","CAP_FACE",FACE,{"disambiguationData":[OSD([sQuery(id+"F0.wireOp",EDGE,"E0"),sQuery(id+"F0.wireOp",EDGE,"E1"),sQuery(id+"F0.wireOp",EDGE,"E2"),sQuery(id+"F0.wireOp",EDGE,"E3"),sQuery(id+"F0.wireOp",EDGE,"E4"),sQuery(id+"F0.wireOp",EDGE,"E6"),sQuery(id+"F0.wireOp",EDGE,"E7"),sQuery(id+"F0.wireOp",EDGE,"E8"),sQuery(id+"F0.wireOp",EDGE,"E9"),sQuery(id+"F0.wireOp",EDGE,"E10"),sQuery(id+"F0.wireOp",EDGE,"E11")])],"isStart":false});
            var sketch = newSketch(context, id + "F42", { "sketchPlane" : qUnion([Q0])});
            skLineSegment(sketch, "E160.bottom", {"start": v(2048.8, 12796.58) * mm, "end": v(2302.8, 12796.58) * mm});
            skLineSegment(sketch, "E160.top", {"start": v(2048.8, 12517.18) * mm, "end": v(2302.8, 12517.18) * mm});
            skLineSegment(sketch, "E160.left", {"start": v(2048.8, 12796.58) * mm, "end": v(2048.8, 12517.18) * mm});
            skLineSegment(sketch, "E160.right", {"start": v(2302.8, 12796.58) * mm, "end": v(2302.8, 12517.18) * mm});
            skSolve(sketch);
        }
        {
            var Q0;
            Q0 = qSketchRegion(id + "F42", true);
            extrude(context, id + "F43", {"entities" : qUnion([Q0]), "depth" : 2286 * mm, "offsetDistance" : 25.4 * mm});
        }
        {
            var Q0;
            Q0=makeQuery(id+"F1.opExtrude","CAP_FACE",FACE,{"disambiguationData":[OSD([sQuery(id+"F0.wireOp",EDGE,"E0"),sQuery(id+"F0.wireOp",EDGE,"E1"),sQuery(id+"F0.wireOp",EDGE,"E2"),sQuery(id+"F0.wireOp",EDGE,"E3"),sQuery(id+"F0.wireOp",EDGE,"E4"),sQuery(id+"F0.wireOp",EDGE,"E6"),sQuery(id+"F0.wireOp",EDGE,"E7"),sQuery(id+"F0.wireOp",EDGE,"E8"),sQuery(id+"F0.wireOp",EDGE,"E9"),sQuery(id+"F0.wireOp",EDGE,"E10"),sQuery(id+"F0.wireOp",EDGE,"E11")])],"isStart":false});
            var sketch = newSketch(context, id + "F44", { "sketchPlane" : qUnion([Q0])});
            skLineSegment(sketch, "E161.bottom", {"start": v(-6816.05, 15508.14) * mm, "end": v(-6536.65, 15508.14) * mm});
            skLineSegment(sketch, "E161.top", {"start": v(-6816.05, 15177.94) * mm, "end": v(-6536.65, 15177.94) * mm});
            skLineSegment(sketch, "E161.left", {"start": v(-6816.05, 15508.14) * mm, "end": v(-6816.05, 15177.94) * mm});
            skLineSegment(sketch, "E161.right", {"start": v(-6536.65, 15508.14) * mm, "end": v(-6536.65, 15177.94) * mm});
            skSolve(sketch);
        }
        {
            var Q0;
            Q0 = qSketchRegion(id + "F44", true);
            extrude(context, id + "F45", {"entities" : qUnion([Q0]), "depth" : 2184.4 * mm, "offsetDistance" : 25.4 * mm});
        }
        {
            var Q0;
            Q0=makeQuery(id+"F7.opExtrude","CAP_FACE",FACE,{"disambiguationData":[OSD([sQuery(id+"F6.wireOp",EDGE,"E142.bottom"),sQuery(id+"F6.wireOp",EDGE,"E142.top"),sQuery(id+"F6.wireOp",EDGE,"E142.left"),sQuery(id+"F6.wireOp",EDGE,"E142.right")])],"isStart":false});
            var sketch = newSketch(context, id + "F46", { "sketchPlane" : qUnion([Q0])});
            skText(sketch, "E162", { "text": "1\n", "fontName": "OpenSans-Bold.ttf"});
            const initialGuessF46  = {"E162": [-5.12769, 8.5158, 1, 0, 0.46204]};
            skSetInitialGuess(sketch, initialGuessF46);
            skSolve(sketch);
        }
        {
            var Q0;
            Q0 = qSketchRegion(id + "F46", true);
            extrude(context, id + "F47", {"entities" : qUnion([Q0]), "operationType" : NewBodyOperationType.ADD, "depth" : 127 * mm, "offsetDistance" : 25.4 * mm});
        }
        {
            var Q0;
            Q0=makeQuery(id+"F19.opExtrude","CAP_FACE",FACE,{"disambiguationData":[OSD([sQuery(id+"F8.wireOp",EDGE,"E143.bottom"),sQuery(id+"F8.wireOp",EDGE,"E143.top"),sQuery(id+"F8.wireOp",EDGE,"E143.left"),sQuery(id+"F8.wireOp",EDGE,"E143.right")])],"isStart":false});
            var sketch = newSketch(context, id + "F48", { "sketchPlane" : qUnion([Q0])});
            skText(sketch, "E163", { "text": "2", "fontName": "OpenSans-Bold.ttf"});
            const initialGuessF48  = {"E163": [-8.4672, 9.4366, 1, 0, 0.82084]};
            skSetInitialGuess(sketch, initialGuessF48);
            skSolve(sketch);
        }
        {
            var Q0;
            Q0 = qSketchRegion(id + "F48", true);
            extrude(context, id + "F49", {"entities" : qUnion([Q0]), "depth" : 127 * mm, "offsetDistance" : 25.4 * mm});
        }
        {
            var Q0;
            Q0=makeQuery(id+"F10.opExtrude","CAP_FACE",FACE,{"disambiguationData":[OSD([sQuery(id+"F9.wireOp",EDGE,"E144.bottom"),sQuery(id+"F9.wireOp",EDGE,"E144.top"),sQuery(id+"F9.wireOp",EDGE,"E144.left"),sQuery(id+"F9.wireOp",EDGE,"E144.right")])],"isStart":false});
            var sketch = newSketch(context, id + "F50", { "sketchPlane" : qUnion([Q0])});
            skText(sketch, "E164", { "text": "3", "fontName": "OpenSans-Bold.ttf"});
            const initialGuessF50  = {"E164": [14.32856, -10.55029, 1, 0, 1.28877]};
            skSetInitialGuess(sketch, initialGuessF50);
            skSolve(sketch);
        }
        {
            var Q0;
            Q0 = qSketchRegion(id + "F50", true);
            extrude(context, id + "F51", {"entities" : qUnion([Q0]), "operationType" : NewBodyOperationType.ADD, "depth" : 127 * mm, "offsetDistance" : 25.4 * mm});
        }
        {
            var Q0;
            Q0=makeQuery(id+"F12.opExtrude","CAP_FACE",FACE,{"disambiguationData":[OSD([sQuery(id+"F11.wireOp",EDGE,"E145.bottom"),sQuery(id+"F11.wireOp",EDGE,"E145.top"),sQuery(id+"F11.wireOp",EDGE,"E145.left"),sQuery(id+"F11.wireOp",EDGE,"E145.right")])],"isStart":false});
            var sketch = newSketch(context, id + "F52", { "sketchPlane" : qUnion([Q0])});
            skText(sketch, "E165", { "text": "4\n", "fontName": "OpenSans-Bold.ttf"});
            const initialGuessF52  = {"E165": [14.48458, -1.524, 1, 0, 1.44398]};
            skSetInitialGuess(sketch, initialGuessF52);
            skSolve(sketch);
        }
        {
            var Q0;
            Q0 = qSketchRegion(id + "F52", true);
            extrude(context, id + "F53", {"entities" : qUnion([Q0]), "operationType" : NewBodyOperationType.ADD, "depth" : 127 * mm, "offsetDistance" : 25.4 * mm});
        }
        {
            var Q0;
            Q0=makeQuery(id+"F14.opExtrude","CAP_FACE",FACE,{"disambiguationData":[OSD([sQuery(id+"F13.wireOp",EDGE,"E146.bottom"),sQuery(id+"F13.wireOp",EDGE,"E146.top"),sQuery(id+"F13.wireOp",EDGE,"E146.left"),sQuery(id+"F13.wireOp",EDGE,"E146.right")])],"isStart":false});
            var sketch = newSketch(context, id + "F54", { "sketchPlane" : qUnion([Q0])});
            skText(sketch, "E166", { "text": "5", "fontName": "OpenSans-Bold.ttf"});
            const initialGuessF54  = {"E166": [14.6612, -3.87445, 1, 0, 1.143]};
            skSetInitialGuess(sketch, initialGuessF54);
            skSolve(sketch);
        }
        {
            var Q0;
            Q0 = qSketchRegion(id + "F54", true);
            extrude(context, id + "F55", {"entities" : qUnion([Q0]), "operationType" : NewBodyOperationType.ADD, "depth" : 127 * mm, "offsetDistance" : 25.4 * mm});
        }
        {
            var Q0;
            Q0=makeQuery(id+"F16.opExtrude","CAP_FACE",FACE,{"disambiguationData":[OSD([sQuery(id+"F15.wireOp",EDGE,"E147.bottom"),sQuery(id+"F15.wireOp",EDGE,"E147.top"),sQuery(id+"F15.wireOp",EDGE,"E147.left"),sQuery(id+"F15.wireOp",EDGE,"E147.right")])],"isStart":false});
            var sketch = newSketch(context, id + "F56", { "sketchPlane" : qUnion([Q0])});
            skText(sketch, "E167", { "text": "6", "fontName": "OpenSans-Regular.ttf"});
            const initialGuessF56  = {"E167": [13.34347, 7.27204, 1, 0, 1.2192]};
            skSetInitialGuess(sketch, initialGuessF56);
            skSolve(sketch);
        }
        {
            var Q0;
            Q0 = qSketchRegion(id + "F56", true);
            extrude(context, id + "F57", {"entities" : qUnion([Q0]), "depth" : 127 * mm, "offsetDistance" : 25.4 * mm});
        }
        {
            var Q0;
            Q0=makeQuery(id+"F18.opExtrude","CAP_FACE",FACE,{"disambiguationData":[OSD([sQuery(id+"F17.wireOp",EDGE,"E148.bottom"),sQuery(id+"F17.wireOp",EDGE,"E148.top"),sQuery(id+"F17.wireOp",EDGE,"E148.left"),sQuery(id+"F17.wireOp",EDGE,"E148.right")])],"isStart":false});
            var sketch = newSketch(context, id + "F58", { "sketchPlane" : qUnion([Q0])});
            skText(sketch, "E168", { "text": "7", "fontName": "OpenSans-Regular.ttf"});
            const initialGuessF58  = {"E168": [14.99951, 7.42903, 1, 0, 0.98553]};
            skSetInitialGuess(sketch, initialGuessF58);
            skSolve(sketch);
        }
        {
            var Q0;
            Q0 = qSketchRegion(id + "F58", true);
            extrude(context, id + "F59", {"entities" : qUnion([Q0]), "depth" : 127 * mm, "offsetDistance" : 25.4 * mm});
        }
        {
            var Q0;
            Q0=makeQuery(id+"F21.opExtrude","CAP_FACE",FACE,{"disambiguationData":[OSD([sQuery(id+"F20.wireOp",EDGE,"E149.bottom"),sQuery(id+"F20.wireOp",EDGE,"E149.top"),sQuery(id+"F20.wireOp",EDGE,"E149.left"),sQuery(id+"F20.wireOp",EDGE,"E149.right")])],"isStart":false});
            var sketch = newSketch(context, id + "F60", { "sketchPlane" : qUnion([Q0])});
            skText(sketch, "E169", { "text": "8", "fontName": "OpenSans-Regular.ttf"});
            const initialGuessF60  = {"E169": [-5.42694, 6.8733, 1, 0, 1.09925]};
            skSetInitialGuess(sketch, initialGuessF60);
            skSolve(sketch);
        }
        {
            var Q0;
            Q0 = qSketchRegion(id + "F60", true);
            extrude(context, id + "F61", {"entities" : qUnion([Q0]), "depth" : 127 * mm, "offsetDistance" : 25.4 * mm});
        }
        {
            var Q0;
            Q0=makeQuery(id+"F23.opExtrude","CAP_FACE",FACE,{"disambiguationData":[OSD([sQuery(id+"F22.wireOp",EDGE,"E150.bottom"),sQuery(id+"F22.wireOp",EDGE,"E150.top"),sQuery(id+"F22.wireOp",EDGE,"E150.left"),sQuery(id+"F22.wireOp",EDGE,"E150.right")])],"isStart":false});
            var sketch = newSketch(context, id + "F62", { "sketchPlane" : qUnion([Q0])});
            skText(sketch, "E170", { "text": "9", "fontName": "OpenSans-Regular.ttf"});
            const initialGuessF62  = {"E170": [6.08578, -1.7837, 1, 0, 0.44895]};
            skSetInitialGuess(sketch, initialGuessF62);
            skSolve(sketch);
        }
        {
            var Q0;
            Q0 = qSketchRegion(id + "F62", true);
            extrude(context, id + "F63", {"entities" : qUnion([Q0]), "depth" : 127 * mm, "offsetDistance" : 25.4 * mm});
        }
        {
            var Q0;
            Q0=makeQuery(id+"F25.opExtrude","CAP_FACE",FACE,{"disambiguationData":[OSD([sQuery(id+"F24.wireOp",EDGE,"E151.bottom"),sQuery(id+"F24.wireOp",EDGE,"E151.top"),sQuery(id+"F24.wireOp",EDGE,"E151.left"),sQuery(id+"F24.wireOp",EDGE,"E151.right")])],"isStart":false});
            var sketch = newSketch(context, id + "F64", { "sketchPlane" : qUnion([Q0])});
            skText(sketch, "E171", { "text": "10\n", "fontName": "OpenSans-Regular.ttf"});
            const initialGuessF64  = {"E171": [-7.99162, 16.29743, 1, 0, 1.86465]};
            skSetInitialGuess(sketch, initialGuessF64);
            skSolve(sketch);
        }
        {
            var Q0;
            Q0 = qSketchRegion(id + "F64", true);
            extrude(context, id + "F65", {"entities" : qUnion([Q0]), "depth" : 127 * mm, "offsetDistance" : 25.4 * mm});
        }
        {
            var Q0;
            Q0=makeQuery(id+"F27.opExtrude","CAP_FACE",FACE,{"disambiguationData":[OSD([sQuery(id+"F26.wireOp",EDGE,"E152.bottom"),sQuery(id+"F26.wireOp",EDGE,"E152.top"),sQuery(id+"F26.wireOp",EDGE,"E152.left"),sQuery(id+"F26.wireOp",EDGE,"E152.right")])],"isStart":false});
            var sketch = newSketch(context, id + "F66", { "sketchPlane" : qUnion([Q0])});
            skText(sketch, "E172", { "text": "11", "fontName": "OpenSans-Regular.ttf"});
            const initialGuessF66  = {"E172": [22.94078, 10.42902, 1, 0, 1.34104]};
            skSetInitialGuess(sketch, initialGuessF66);
            skSolve(sketch);
        }
        {
            var Q0;
            Q0 = qSketchRegion(id + "F66", true);
            extrude(context, id + "F67", {"entities" : qUnion([Q0]), "depth" : 127 * mm, "offsetDistance" : 25.4 * mm});
        }
        {
            var Q0;
            Q0=makeQuery(id+"F29.opExtrude","CAP_FACE",FACE,{"disambiguationData":[OSD([sQuery(id+"F28.wireOp",EDGE,"E153.bottom"),sQuery(id+"F28.wireOp",EDGE,"E153.top"),sQuery(id+"F28.wireOp",EDGE,"E153.left"),sQuery(id+"F28.wireOp",EDGE,"E153.right")])],"isStart":false});
            var sketch = newSketch(context, id + "F68", { "sketchPlane" : qUnion([Q0])});
            skText(sketch, "E173", { "text": "12", "fontName": "OpenSans-Regular.ttf"});
            const initialGuessF68  = {"E173": [25.7137, 10.34728, 1, 0, 1.30773]};
            skSetInitialGuess(sketch, initialGuessF68);
            skSolve(sketch);
        }
        {
            var Q0;
            Q0 = qSketchRegion(id + "F68", true);
            extrude(context, id + "F69", {"entities" : qUnion([Q0]), "depth" : 127 * mm, "offsetDistance" : 25.4 * mm});
        }
        {
            var Q0;
            Q0=makeQuery(id+"F31.opExtrude","CAP_FACE",FACE,{"disambiguationData":[OSD([sQuery(id+"F30.wireOp",EDGE,"E154.bottom"),sQuery(id+"F30.wireOp",EDGE,"E154.top"),sQuery(id+"F30.wireOp",EDGE,"E154.left"),sQuery(id+"F30.wireOp",EDGE,"E154.right")])],"isStart":false});
            var sketch = newSketch(context, id + "F70", { "sketchPlane" : qUnion([Q0])});
            skText(sketch, "E174", { "text": "14\n", "fontName": "OpenSans-Regular.ttf"});
            const initialGuessF70  = {"E174": [-9.379, 13.24372, 1, 0, 0.82873]};
            skSetInitialGuess(sketch, initialGuessF70);
            skSolve(sketch);
        }
        {
            var Q0;
            Q0 = qSketchRegion(id + "F70", true);
            extrude(context, id + "F71", {"entities" : qUnion([Q0]), "depth" : 127 * mm, "offsetDistance" : 25.4 * mm});
        }
        {
            var Q0;
            Q0=makeQuery(id+"F33.opExtrude","CAP_FACE",FACE,{"disambiguationData":[OSD([sQuery(id+"F32.wireOp",EDGE,"E155.bottom"),sQuery(id+"F32.wireOp",EDGE,"E155.top"),sQuery(id+"F32.wireOp",EDGE,"E155.left"),sQuery(id+"F32.wireOp",EDGE,"E155.right")])],"isStart":false});
            var sketch = newSketch(context, id + "F72", { "sketchPlane" : qUnion([Q0])});
            skText(sketch, "E175", { "text": "15", "fontName": "OpenSans-Regular.ttf"});
            const initialGuessF72  = {"E175": [0.98652, 13.798, 1, 0, 1.55516]};
            skSetInitialGuess(sketch, initialGuessF72);
            skSolve(sketch);
        }
        {
            var Q0;
            Q0 = qSketchRegion(id + "F72", true);
            extrude(context, id + "F73", {"entities" : qUnion([Q0]), "operationType" : NewBodyOperationType.ADD, "depth" : 127 * mm, "offsetDistance" : 25.4 * mm});
        }
        {
            var Q0;
            Q0=makeQuery(id+"F35.opExtrude","CAP_FACE",FACE,{"disambiguationData":[OSD([sQuery(id+"F34.wireOp",EDGE,"E156.bottom"),sQuery(id+"F34.wireOp",EDGE,"E156.top"),sQuery(id+"F34.wireOp",EDGE,"E156.left"),sQuery(id+"F34.wireOp",EDGE,"E156.right")])],"isStart":false});
            var sketch = newSketch(context, id + "F74", { "sketchPlane" : qUnion([Q0])});
            skText(sketch, "E176", { "text": "16", "fontName": "OpenSans-Regular.ttf"});
            const initialGuessF74  = {"E176": [-0.16058, 15.36044, 1, 0, 0.42215]};
            skSetInitialGuess(sketch, initialGuessF74);
            skSolve(sketch);
        }
        {
            var Q0;
            Q0 = qSketchRegion(id + "F74", true);
            extrude(context, id + "F75", {"entities" : qUnion([Q0]), "depth" : 127 * mm, "offsetDistance" : 25.4 * mm});
        }
        {
            var Q0;
            Q0=makeQuery(id+"F39.opExtrude","CAP_FACE",FACE,{"disambiguationData":[OSD([sQuery(id+"F38.wireOp",EDGE,"E158.bottom"),sQuery(id+"F38.wireOp",EDGE,"E158.top"),sQuery(id+"F38.wireOp",EDGE,"E158.left"),sQuery(id+"F38.wireOp",EDGE,"E158.right")])],"isStart":false});
            var sketch = newSketch(context, id + "F76", { "sketchPlane" : qUnion([Q0])});
            skText(sketch, "E177", { "text": "17\n", "fontName": "OpenSans-Regular.ttf"});
            const initialGuessF76  = {"E177": [1.1039, 16.42475, 1, 0, 1.55457]};
            skSetInitialGuess(sketch, initialGuessF76);
            skSolve(sketch);
        }
        {
            var Q0;
            Q0 = qSketchRegion(id + "F76", true);
            extrude(context, id + "F77", {"entities" : qUnion([Q0]), "operationType" : NewBodyOperationType.ADD, "depth" : 127 * mm, "offsetDistance" : 25.4 * mm});
        }
        {
            var Q0;
            Q0=makeQuery(id+"F37.opExtrude","CAP_FACE",FACE,{"disambiguationData":[OSD([sQuery(id+"F36.wireOp",EDGE,"E157.bottom"),sQuery(id+"F36.wireOp",EDGE,"E157.top"),sQuery(id+"F36.wireOp",EDGE,"E157.left"),sQuery(id+"F36.wireOp",EDGE,"E157.right")])],"isStart":false});
            var sketch = newSketch(context, id + "F78", { "sketchPlane" : qUnion([Q0])});
            skText(sketch, "E178", { "text": "18\n", "fontName": "OpenSans-Regular.ttf"});
            const initialGuessF78  = {"E178": [-8.18848, 4.3047, 1, 0, 0.77392]};
            skSetInitialGuess(sketch, initialGuessF78);
            skSolve(sketch);
        }
        {
            var Q0;
            Q0 = qSketchRegion(id + "F78", true);
            extrude(context, id + "F79", {"entities" : qUnion([Q0]), "operationType" : NewBodyOperationType.ADD, "depth" : 127 * mm, "offsetDistance" : 25.4 * mm});
        }
        {
            var Q0;
            Q0=makeQuery(id+"F1.opExtrude","CAP_FACE",FACE,{"disambiguationData":[OSD([sQuery(id+"F0.wireOp",EDGE,"E0"),sQuery(id+"F0.wireOp",EDGE,"E1"),sQuery(id+"F0.wireOp",EDGE,"E2"),sQuery(id+"F0.wireOp",EDGE,"E3"),sQuery(id+"F0.wireOp",EDGE,"E4"),sQuery(id+"F0.wireOp",EDGE,"E6"),sQuery(id+"F0.wireOp",EDGE,"E7"),sQuery(id+"F0.wireOp",EDGE,"E8"),sQuery(id+"F0.wireOp",EDGE,"E9"),sQuery(id+"F0.wireOp",EDGE,"E10"),sQuery(id+"F0.wireOp",EDGE,"E11")])],"isStart":false});
            var sketch = newSketch(context, id + "F80", { "sketchPlane" : qUnion([Q0])});
            skLineSegment(sketch, "E179.bottom", {"start": v(-8134.72, 8691.09) * mm, "end": v(-6915.52, 8691.09) * mm});
            skLineSegment(sketch, "E179.top", {"start": v(-8134.72, 6252.69) * mm, "end": v(-6915.52, 6252.69) * mm});
            skLineSegment(sketch, "E179.left", {"start": v(-8134.72, 8691.09) * mm, "end": v(-8134.72, 6252.69) * mm});
            skLineSegment(sketch, "E179.right", {"start": v(-6915.52, 8691.09) * mm, "end": v(-6915.52, 6252.69) * mm});
            skSolve(sketch);
        }
        {
            var Q0;
            Q0 = qSketchRegion(id + "F80", true);
            extrude(context, id + "F81", {"entities" : qUnion([Q0]), "depth" : 2133.6 * mm, "offsetDistance" : 25.4 * mm});
        }
        {
            var Q0;
            Q0=makeQuery(id+"F81.opExtrude","CAP_FACE",FACE,{"disambiguationData":[OSD([sQuery(id+"F80.wireOp",EDGE,"E179.bottom"),sQuery(id+"F80.wireOp",EDGE,"E179.top"),sQuery(id+"F80.wireOp",EDGE,"E179.left"),sQuery(id+"F80.wireOp",EDGE,"E179.right")])],"isStart":false});
            var sketch = newSketch(context, id + "F82", { "sketchPlane" : qUnion([Q0])});
            skText(sketch, "E180", { "text": "19\n", "fontName": "OpenSans-Regular.ttf"});
            const initialGuessF82  = {"E180": [-8.00265, 7.52824, 1, 0, 0.57473]};
            skSetInitialGuess(sketch, initialGuessF82);
            skSolve(sketch);
        }
        {
            var Q0;
            Q0 = qSketchRegion(id + "F82", true);
            extrude(context, id + "F83", {"entities" : qUnion([Q0]), "operationType" : NewBodyOperationType.ADD, "depth" : 127 * mm, "offsetDistance" : 25.4 * mm});
        }
        {
            var Q0;
            Q0=makeQuery(id+"F41.opExtrude","CAP_FACE",FACE,{"disambiguationData":[OSD([sQuery(id+"F40.wireOp",EDGE,"E159.bottom"),sQuery(id+"F40.wireOp",EDGE,"E159.top"),sQuery(id+"F40.wireOp",EDGE,"E159.left"),sQuery(id+"F40.wireOp",EDGE,"E159.right")])],"isStart":false});
            var sketch = newSketch(context, id + "F84", { "sketchPlane" : qUnion([Q0])});
            skText(sketch, "E181", { "text": "20", "fontName": "OpenSans-Regular.ttf"});
            const initialGuessF84  = {"E181": [0.01982, 16.97542, 1, 0, 0.27046]};
            skSetInitialGuess(sketch, initialGuessF84);
            skSolve(sketch);
        }
        {
            var Q0;
            Q0 = qSketchRegion(id + "F84", true);
            extrude(context, id + "F85", {"entities" : qUnion([Q0]), "depth" : 127 * mm, "offsetDistance" : 25.4 * mm});
        }
        {
            var Q0;
            Q0=makeQuery(id+"F43.opExtrude","CAP_FACE",FACE,{"disambiguationData":[OSD([sQuery(id+"F42.wireOp",EDGE,"E160.bottom"),sQuery(id+"F42.wireOp",EDGE,"E160.top"),sQuery(id+"F42.wireOp",EDGE,"E160.left"),sQuery(id+"F42.wireOp",EDGE,"E160.right")])],"isStart":false});
            var sketch = newSketch(context, id + "F86", { "sketchPlane" : qUnion([Q0])});
            skText(sketch, "E182", { "text": "21\n", "fontName": "OpenSans-Regular.ttf"});
            const initialGuessF86  = {"E182": [2.10119, 12.61264, 1, 0, 0.13443]};
            skSetInitialGuess(sketch, initialGuessF86);
            skSolve(sketch);
        }
        {
            var Q0;
            Q0 = qSketchRegion(id + "F86", true);
            extrude(context, id + "F87", {"entities" : qUnion([Q0]), "depth" : 127 * mm, "offsetDistance" : 25.4 * mm});
        }
        {
            var Q0;
            Q0=makeQuery(id+"F45.opExtrude","CAP_FACE",FACE,{"disambiguationData":[OSD([sQuery(id+"F44.wireOp",EDGE,"E161.bottom"),sQuery(id+"F44.wireOp",EDGE,"E161.top"),sQuery(id+"F44.wireOp",EDGE,"E161.left"),sQuery(id+"F44.wireOp",EDGE,"E161.right")])],"isStart":false});
            var sketch = newSketch(context, id + "F88", { "sketchPlane" : qUnion([Q0])});
            skText(sketch, "E183", { "text": "22", "fontName": "OpenSans-Regular.ttf"});
            const initialGuessF88  = {"E183": [-6.78914, 15.29685, 1, 0, 0.13988]};
            skSetInitialGuess(sketch, initialGuessF88);
            skSolve(sketch);
        }
        {
            var Q0;
            Q0 = qSketchRegion(id + "F88", true);
            extrude(context, id + "F89", {"entities" : qUnion([Q0]), "depth" : 127 * mm, "offsetDistance" : 25.4 * mm});
        }
    });
